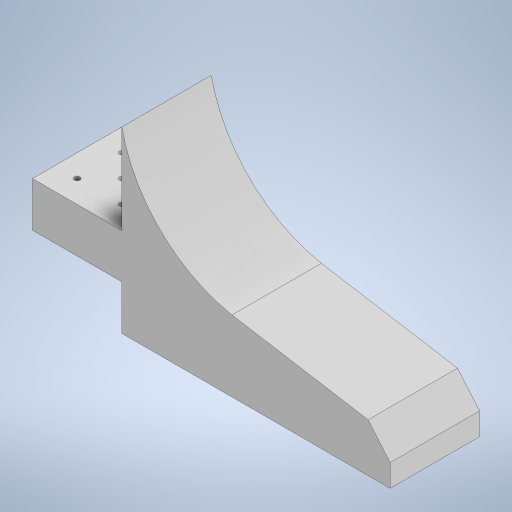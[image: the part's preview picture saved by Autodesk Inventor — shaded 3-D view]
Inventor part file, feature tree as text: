
AUTODESK INVENTOR PART (.ipt)
format: ipt  version: 2023 (Build 270158000, 158)  size: 249,344 bytes
history: native  units: in
note: dims shown in document units (in); Inventor stores cm internally (conversion verified against a paired STEP export)
features: extrude x2, sketch x2, chamfer x1
ambient origin geometry x8: Origin, YZ Plane, XZ Plane, XY Plane, X Axis, Y Axis, Z Axis, Center Point
bodies: Solid1 (feature_tree)
feature tree (5):
  extrude  "Extrusion1"  Depth=16.0in
  chamfer  "Chamfer1"  Distance=2.0in
  extrude  "Extrusion2"  Depth=4.0in TaperAngle=0.0deg
  sketch  "Sketch1"  dims[d0=16.0in d1=8.0in]
  sketch  "Sketch2"  dims[d2=4.0in d3=2.0in d4=4.0in d5=0.0in d6=1.0in d7=0.125in d8=45.0deg d9=0.25in d10=0.25in d11=0.25in d12=0.25in d13=0.25in d14=1.0in d15=1.0in d16=1.0in d17=1.0in d18=1.0in d19=1.0in d20=1.0in d21=1.0in d22=2.0in d23=2.0in d24=4.0in d25=0.0in d26=4.0in]
